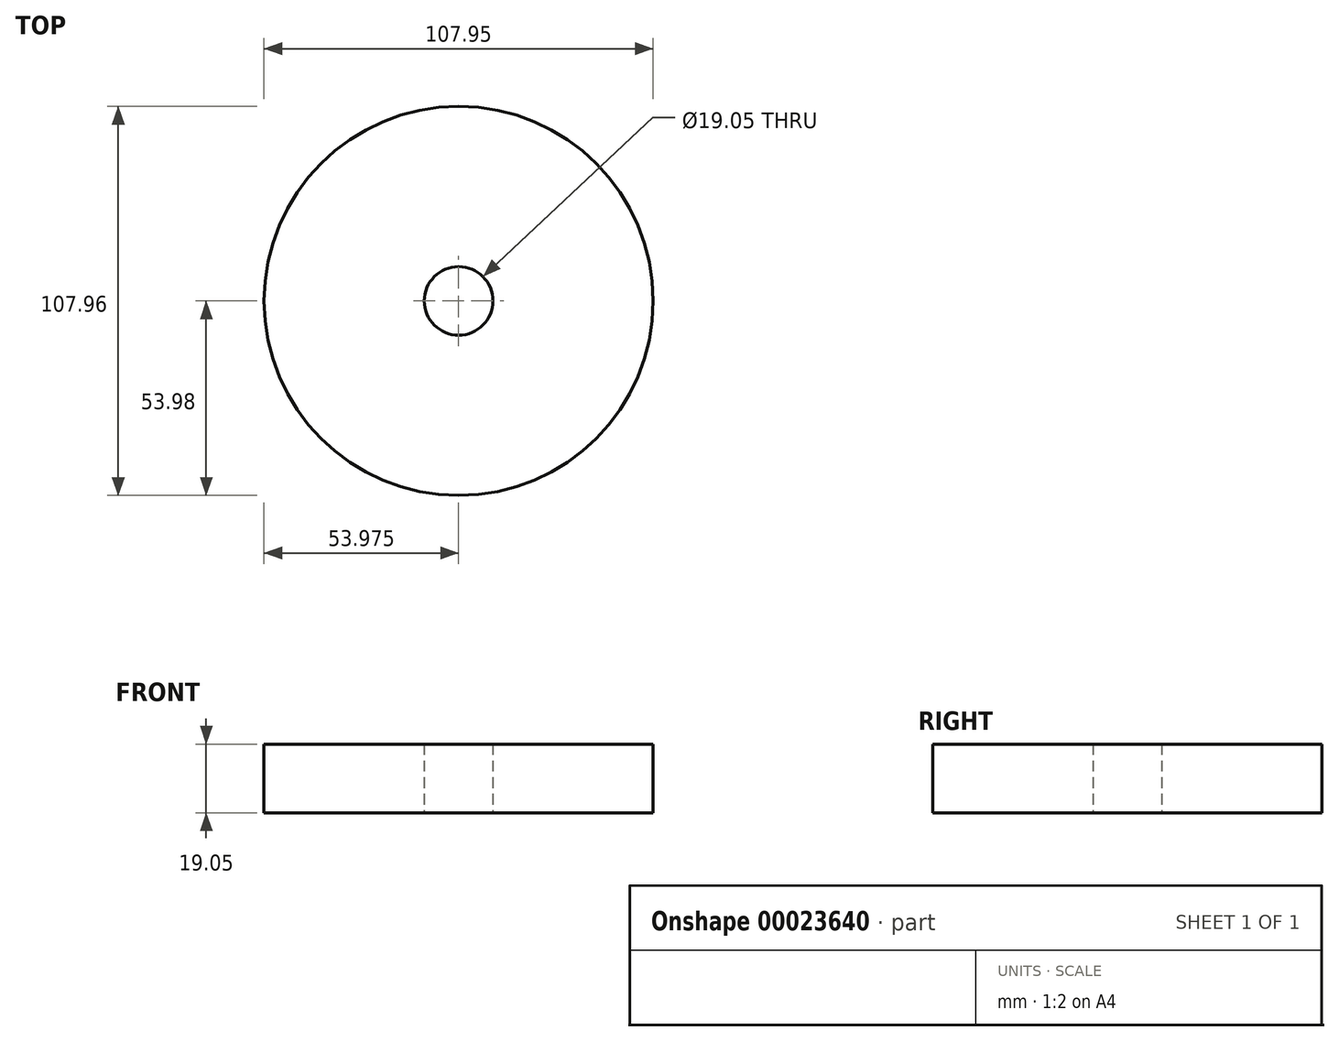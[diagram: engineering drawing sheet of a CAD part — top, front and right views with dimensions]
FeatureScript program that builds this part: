
annotation { "Feature Type Name" : "Feature", "Feature Type Description" : "" }
export const myFeature = defineFeature(function(context is Context, id is Id, definition is map)
    precondition{}
    {
        {
            var Q0;
            Q0=qCreatedBy(makeId("Front.planeOp"),FACE);
            var sketch = newSketch(context, id + "F0", { "sketchPlane" : qUnion([Q0])});
            skLineSegment(sketch, "E0.bottom", {"start": v(0, 0) * mm, "end": v(44.45, 0) * mm});
            skLineSegment(sketch, "E0.top", {"start": v(0, 19.05) * mm, "end": v(44.45, 19.05) * mm});
            skLineSegment(sketch, "E0.left", {"start": v(0, 0) * mm, "end": v(0, 19.05) * mm});
            skLineSegment(sketch, "E0.right", {"start": v(44.45, 0) * mm, "end": v(44.45, 19.05) * mm});
            skLineSegment(sketch, "E1.bottom", {"start": v(0, 19.05) * mm, "end": v(25.4, 19.05) * mm});
            skLineSegment(sketch, "E1.top", {"start": v(0, 76.2) * mm, "end": v(25.4, 76.2) * mm});
            skLineSegment(sketch, "E1.left", {"start": v(0, 19.05) * mm, "end": v(0, 76.2) * mm});
            skLineSegment(sketch, "E1.right", {"start": v(25.4, 19.05) * mm, "end": v(25.4, 76.2) * mm});
            skLineSegment(sketch, "E2.bottom", {"start": v(0, 76.2) * mm, "end": v(19.05, 76.2) * mm});
            skLineSegment(sketch, "E2.top", {"start": v(0, 88.9) * mm, "end": v(19.05, 88.9) * mm});
            skLineSegment(sketch, "E2.left", {"start": v(0, 76.2) * mm, "end": v(0, 88.9) * mm});
            skLineSegment(sketch, "E2.right", {"start": v(19.05, 76.2) * mm, "end": v(19.05, 88.9) * mm});
            skLineSegment(sketch, "E3", {"start": v(-9.52, 0) * mm, "end": v(-9.52, 159.3) * mm, "construction": true});
            skSolve(sketch);
        }
        {
            var Q0;
            Q0=makeQuery(id+"F0.imprint","IMPRINT",FACE,{"disambiguationData":[TD([[makeQuery(id+"F0.imprint","IMPRINT",EDGE,{"derivedFrom":sQuery(id+"F0.wireOp",EDGE,"E0.bottom")}),1.0]])]});
            var Q1;
            Q1=makeQuery(id+"F0.imprint","IMPRINT",FACE,{"disambiguationData":[TD([[makeQuery(id+"F0.imprint","IMPRINT",EDGE,{"derivedFrom":sQuery(id+"F0.wireOp",EDGE,"E2.bottom")}),1.0]])]});
            var Q2;
            Q2=makeQuery(id+"F0.imprint","IMPRINT",FACE,{"disambiguationData":[TD([[makeQuery(id+"F0.imprint","IMPRINT",EDGE,{"derivedFrom":sQuery(id+"F0.wireOp",EDGE,"E1.bottom")}),1.0]])]});
            var Q3;
            Q3=sQuery(id+"F0.wireOp",EDGE,"E3");
            revolve(context, id + "F1", {"entities" : qUnion([Q0, Q1, Q2]), "axis" : qUnion([Q3]), "revolveType" : RevolveType.FULL});
        }
    });
